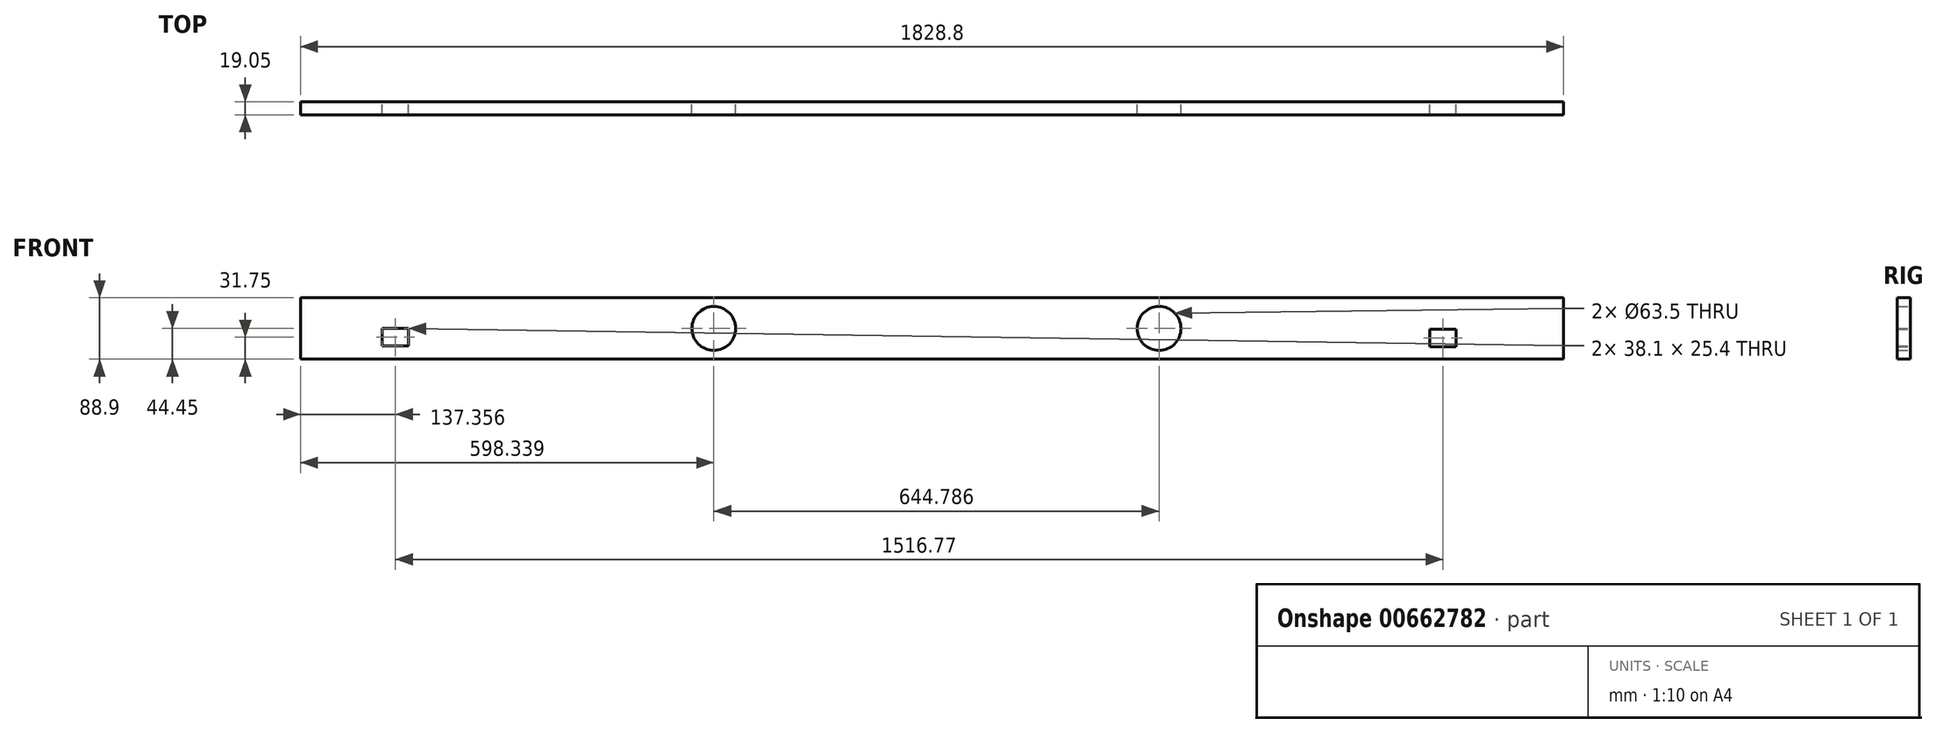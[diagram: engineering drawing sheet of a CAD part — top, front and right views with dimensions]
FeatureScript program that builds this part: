
annotation { "Feature Type Name" : "Feature", "Feature Type Description" : "" }
export const myFeature = defineFeature(function(context is Context, id is Id, definition is map)
    precondition{}
    {
        {
            var Q0;
            Q0=qCreatedBy(makeId("Front.planeOp"),FACE);
            var sketch = newSketch(context, id + "F0", { "sketchPlane" : qUnion([Q0])});
            skLineSegment(sketch, "E0.bottom", {"start": v(914.4, -44.45) * mm, "end": v(-914.4, -44.45) * mm});
            skLineSegment(sketch, "E0.top", {"start": v(914.4, 44.45) * mm, "end": v(-914.4, 44.45) * mm});
            skLineSegment(sketch, "E0.left", {"start": v(914.4, -44.45) * mm, "end": v(914.4, 44.45) * mm});
            skLineSegment(sketch, "E0.right", {"start": v(-914.4, -44.45) * mm, "end": v(-914.4, 44.45) * mm});
            skPoint(sketch, "E0.middle", {"position": v(0, 0) * mm});
            skCircle(sketch, "E1", {"center": v(-316.06, 0) * mm, "radius": 31.75 * mm});
            skCircle(sketch, "E2", {"center": v(328.73, 0) * mm, "radius": 31.75 * mm});
            skLineSegment(sketch, "E3.bottom", {"start": v(-796.1, 0) * mm, "end": v(-758, 0) * mm});
            skLineSegment(sketch, "E3.top", {"start": v(-796.1, -25.4) * mm, "end": v(-758, -25.4) * mm});
            skLineSegment(sketch, "E3.left", {"start": v(-796.1, 0) * mm, "end": v(-796.1, -25.4) * mm});
            skLineSegment(sketch, "E3.right", {"start": v(-758, 0) * mm, "end": v(-758, -25.4) * mm});
            skLineSegment(sketch, "E4.bottom", {"start": v(720.68, -1.19) * mm, "end": v(758.78, -1.19) * mm});
            skLineSegment(sketch, "E4.top", {"start": v(720.68, -26.59) * mm, "end": v(758.78, -26.59) * mm});
            skLineSegment(sketch, "E4.left", {"start": v(720.68, -1.19) * mm, "end": v(720.68, -26.59) * mm});
            skLineSegment(sketch, "E4.right", {"start": v(758.78, -1.19) * mm, "end": v(758.78, -26.59) * mm});
            skSolve(sketch);
        }
        {
            var Q0;
            Q0=makeQuery(id+"F0.imprint","IMPRINT",FACE,{"disambiguationData":[TD([[makeQuery(id+"F0.imprint","IMPRINT",EDGE,{"derivedFrom":sQuery(id+"F0.wireOp",EDGE,"E0.bottom")}),-1.0]])]});
            extrude(context, id + "F1", {"entities" : qUnion([Q0]), "depth" : 19.05 * mm, "offsetDistance" : 25.4 * mm});
        }
    });
